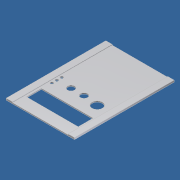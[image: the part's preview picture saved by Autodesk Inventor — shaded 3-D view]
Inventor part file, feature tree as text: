
AUTODESK INVENTOR PART (.ipt)
format: ipt  version: unknown  size: 225,280 bytes
history: native  units: mm
features: extrude x3, sketch x3
ambient origin geometry x8: Origin, YZ Plane, XZ Plane, XY Plane, X Axis, Y Axis, Z Axis, Center Point
bodies: Volumenkörper1 (feature_tree)
feature tree (6):
  extrude  "Extrusion1"  Depth=100.0mm
  extrude  "Extrusion2"  Depth=1.65mm
  extrude  "Extrusion3"  Depth=6.4mm
  sketch  "Skizze1"  dims[d0=68.6mm d1=100.0mm]
  sketch  "Skizze2"  dims[d2=65.3mm d3=1.65mm]
  sketch  "Skizze3"  dims[d4=1.1mm d5=0.0mm d6=6.4mm d7=6.4mm d8=0.7mm d9=0.0mm d10=52.0mm d11=8.3mm d12=68.6mm d13=100.0mm d14=15.0mm d15=12.0mm d22=3.0mm d23=3.0mm d24=3.0mm d25=42.0mm d26=42.0mm d27=42.0mm d28=17.5mm d29=10.5mm d30=7.0mm d31=7.0mm d32=36.7mm d33=5.0mm d34=5.0mm d35=0.7mm d36=0.0mm d37=35.0mm d38=38.5mm d39=38.5mm d40=28.0mm d41=15.0mm]
